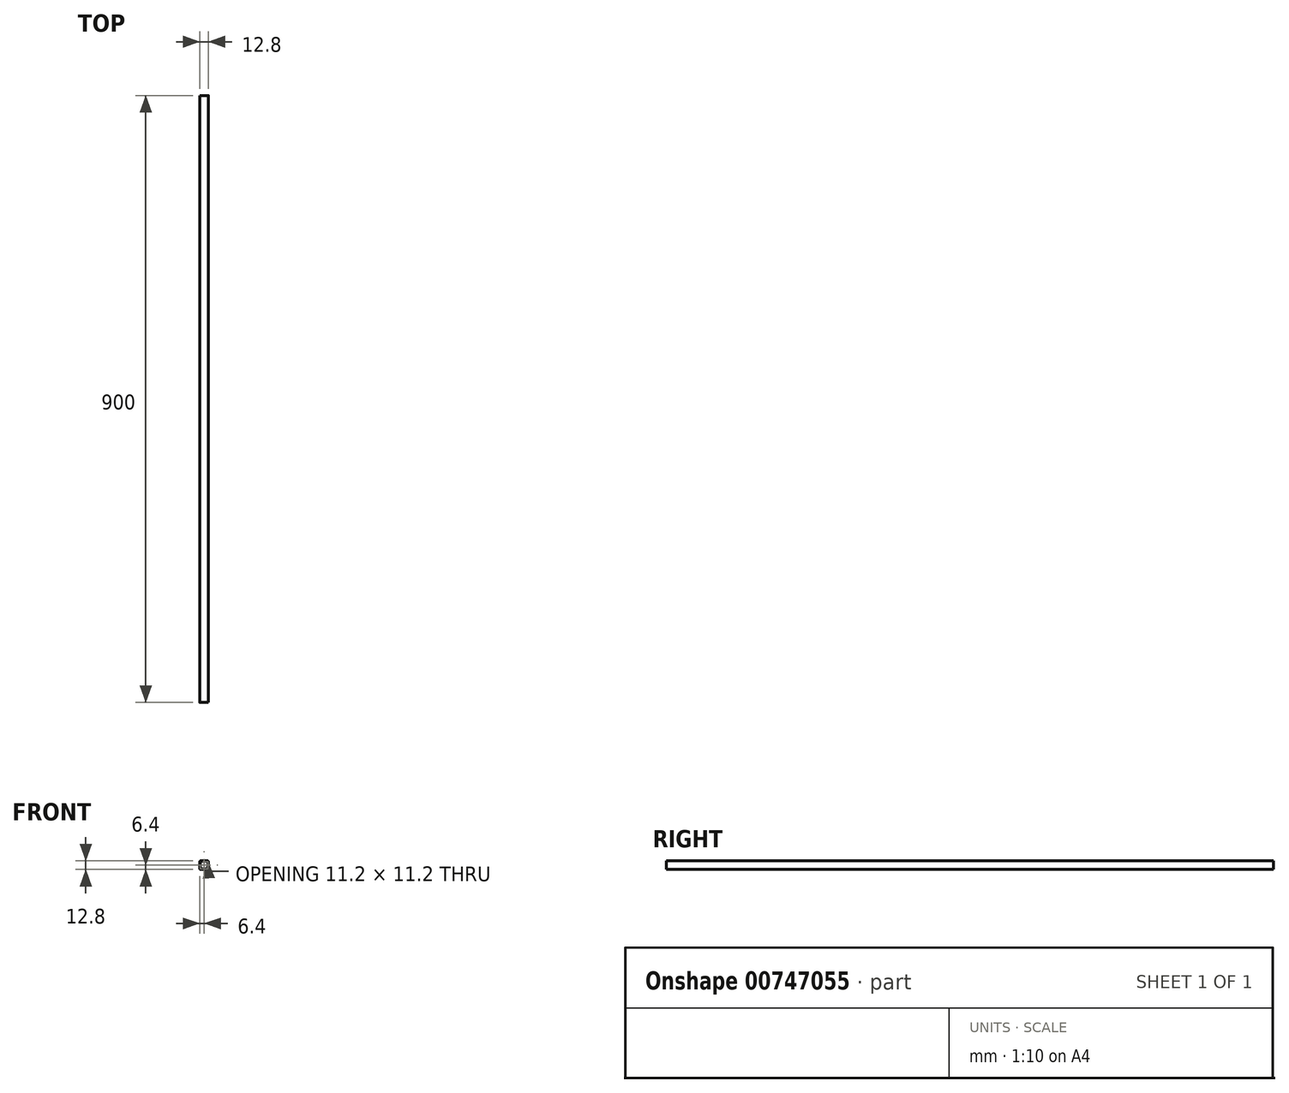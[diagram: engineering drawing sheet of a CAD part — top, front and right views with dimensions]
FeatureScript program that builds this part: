
annotation { "Feature Type Name" : "Feature", "Feature Type Description" : "" }
export const myFeature = defineFeature(function(context is Context, id is Id, definition is map)
    precondition{}
    {
        {
            var Q0;
            Q0=qCreatedBy(makeId("Front.planeOp"),FACE);
            var sketch = newSketch(context, id + "F0", { "sketchPlane" : qUnion([Q0])});
            skLineSegment(sketch, "E0.bottom", {"start": v(-5.2, 6.4) * mm, "end": v(5.2, 6.4) * mm});
            skLineSegment(sketch, "E0.top", {"start": v(-5.2, -6.4) * mm, "end": v(5.2, -6.4) * mm});
            skLineSegment(sketch, "E0.left", {"start": v(-6.4, 5.2) * mm, "end": v(-6.4, -5.2) * mm});
            skLineSegment(sketch, "E0.right", {"start": v(6.4, 5.2) * mm, "end": v(6.4, -5.2) * mm});
            skPoint(sketch, "E0.middle", {"position": v(0, 0) * mm});
            skPoint(sketch, "E1.visualSharp", {"position": v(-6.4, 6.4) * mm});
            skArc(sketch, "E1.filletArc", {"start": v(-5.2, 6.4) * mm, "mid": v(-6.05, 6.05) * mm, "end": v(-6.4, 5.2) * mm});
            skPoint(sketch, "E2.visualSharp", {"position": v(6.4, 6.4) * mm});
            skArc(sketch, "E2.filletArc", {"start": v(6.4, 5.2) * mm, "mid": v(6.05, 6.05) * mm, "end": v(5.2, 6.4) * mm});
            skPoint(sketch, "E3.visualSharp", {"position": v(6.4, -6.4) * mm});
            skArc(sketch, "E3.filletArc", {"start": v(5.2, -6.4) * mm, "mid": v(6.05, -6.05) * mm, "end": v(6.4, -5.2) * mm});
            skPoint(sketch, "E4.visualSharp", {"position": v(-6.4, -6.4) * mm});
            skArc(sketch, "E4.filletArc", {"start": v(-6.4, -5.2) * mm, "mid": v(-6.05, -6.05) * mm, "end": v(-5.2, -6.4) * mm});
            skLineSegment(sketch, "E5.0", {"start": v(-5.2, 5.6) * mm, "end": v(5.2, 5.6) * mm});
            skLineSegment(sketch, "E5.1", {"start": v(-5.6, 5.2) * mm, "end": v(-5.6, -5.2) * mm});
            skLineSegment(sketch, "E5.2", {"start": v(-5.2, -5.6) * mm, "end": v(5.2, -5.6) * mm});
            skLineSegment(sketch, "E5.3", {"start": v(5.6, 5.2) * mm, "end": v(5.6, -5.2) * mm});
            skPoint(sketch, "E6.visualSharp", {"position": v(-5.6, 5.6) * mm});
            skArc(sketch, "E6.filletArc", {"start": v(-5.2, 5.6) * mm, "mid": v(-5.48, 5.48) * mm, "end": v(-5.6, 5.2) * mm});
            skPoint(sketch, "E7.visualSharp", {"position": v(5.6, 5.6) * mm});
            skArc(sketch, "E7.filletArc", {"start": v(5.6, 5.2) * mm, "mid": v(5.48, 5.48) * mm, "end": v(5.2, 5.6) * mm});
            skPoint(sketch, "E8.visualSharp", {"position": v(5.6, -5.6) * mm});
            skArc(sketch, "E8.filletArc", {"start": v(5.2, -5.6) * mm, "mid": v(5.48, -5.48) * mm, "end": v(5.6, -5.2) * mm});
            skPoint(sketch, "E9.visualSharp", {"position": v(-5.6, -5.6) * mm});
            skArc(sketch, "E9.filletArc", {"start": v(-5.6, -5.2) * mm, "mid": v(-5.48, -5.48) * mm, "end": v(-5.2, -5.6) * mm});
            skSolve(sketch);
        }
        {
            var Q0;
            Q0=qCreatedBy(makeId("Front.planeOp"),FACE);
            cPlane(context, id + "F1", {"entities" : qUnion([Q0]), "cplaneType" : CPlaneType.OFFSET, "offset" : 438 * mm, "oppositeDirection" : true, "width" : 150 * mm, "height" : 150 * mm});
        }
        {
            var Q0;
            Q0=makeQuery(id+"F0.imprint","IMPRINT",FACE,{"disambiguationData":[TD([[makeQuery(id+"F0.imprint","IMPRINT",EDGE,{"derivedFrom":sQuery(id+"F0.wireOp",EDGE,"E0.bottom")}),-1.0]])]});
            extrude(context, id + "F2", {"entities" : qUnion([Q0]), "oppositeDirection" : true, "depth" : 500 * mm, "offsetDistance" : 25 * mm});
        }
        {
            var Q0;
            Q0=makeQuery(id+"F2.opExtrude","CAP_FACE",FACE,{"disambiguationData":[OSD([sQuery(id+"F0.wireOp",EDGE,"E0.bottom"),sQuery(id+"F0.wireOp",EDGE,"E0.top"),sQuery(id+"F0.wireOp",EDGE,"E0.left"),sQuery(id+"F0.wireOp",EDGE,"E0.right"),sQuery(id+"F0.wireOp",EDGE,"E1.filletArc"),sQuery(id+"F0.wireOp",EDGE,"E2.filletArc"),sQuery(id+"F0.wireOp",EDGE,"E3.filletArc"),sQuery(id+"F0.wireOp",EDGE,"E4.filletArc"),sQuery(id+"F0.wireOp",EDGE,"E5.0"),sQuery(id+"F0.wireOp",EDGE,"E5.1"),sQuery(id+"F0.wireOp",EDGE,"E5.2"),sQuery(id+"F0.wireOp",EDGE,"E5.3"),sQuery(id+"F0.wireOp",EDGE,"E6.filletArc"),sQuery(id+"F0.wireOp",EDGE,"E7.filletArc"),sQuery(id+"F0.wireOp",EDGE,"E8.filletArc"),sQuery(id+"F0.wireOp",EDGE,"E9.filletArc")])],"isStart":true});
            extrude(context, id + "F3", {"entities" : qUnion([Q0]), "operationType" : NewBodyOperationType.ADD, "depth" : 400 * mm, "offsetDistance" : 25 * mm});
        }
    });
